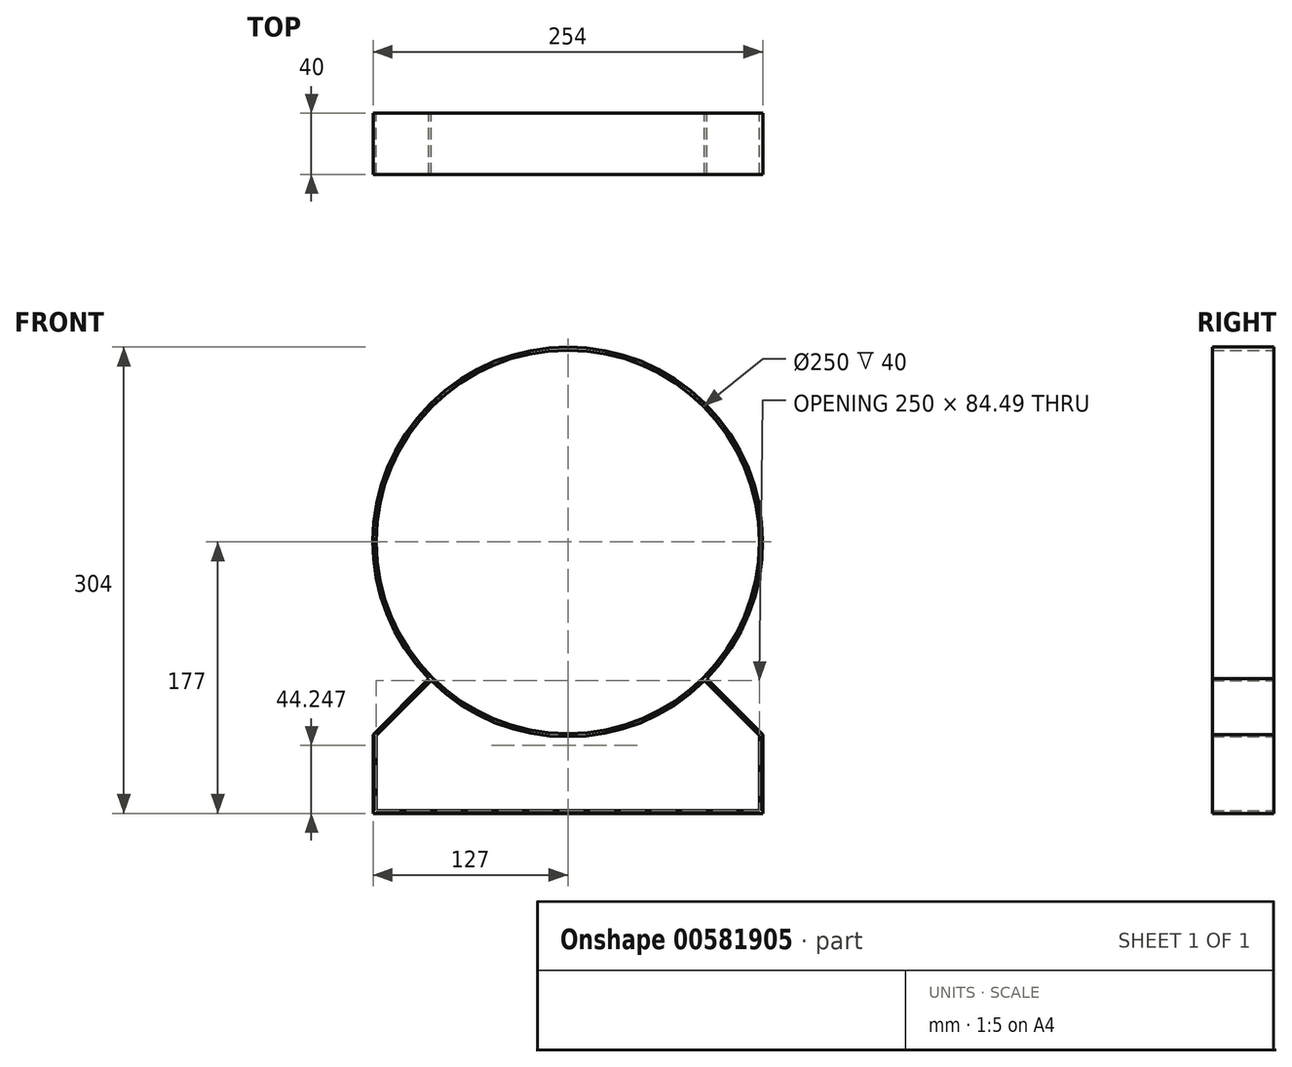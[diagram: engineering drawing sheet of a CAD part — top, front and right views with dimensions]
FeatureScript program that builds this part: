
annotation { "Feature Type Name" : "Feature", "Feature Type Description" : "" }
export const myFeature = defineFeature(function(context is Context, id is Id, definition is map)
    precondition{}
    {
        {
            var Q0;
            Q0=qCreatedBy(makeId("Front.planeOp"),FACE);
            var sketch = newSketch(context, id + "F0", { "sketchPlane" : qUnion([Q0])});
            skLineSegment(sketch, "E0", {"start": v(0, 0) * mm, "end": v(-679.96, 0) * mm, "construction": true});
            skLineSegment(sketch, "E1", {"start": v(0, 0) * mm, "end": v(0, 658.78) * mm, "construction": true});
            skLineSegment(sketch, "E2", {"start": v(0, 0) * mm, "end": v(-291.77, -291.77) * mm, "construction": true});
            skLineSegment(sketch, "E3", {"start": v(0, 0) * mm, "end": v(291.77, -291.77) * mm, "construction": true});
            skCircle(sketch, "E4", {"center": v(0, 0) * mm, "radius": 125 * mm});
            skCircle(sketch, "E5", {"center": v(0, 0) * mm, "radius": 127 * mm});
            skLineSegment(sketch, "E6", {"start": v(-127, -177) * mm, "end": v(0, -177) * mm});
            skLineSegment(sketch, "E7", {"start": v(-125, -175) * mm, "end": v(0, -175) * mm});
            skLineSegment(sketch, "E8", {"start": v(0, 0) * mm, "end": v(0, -311.11) * mm, "construction": true});
            skLineSegment(sketch, "E9", {"start": v(-125, -175) * mm, "end": v(-125, -126.41) * mm});
            skLineSegment(sketch, "E10", {"start": v(-127, -177) * mm, "end": v(-127, -125.59) * mm});
            skLineSegment(sketch, "E11", {"start": v(-90.5, -89.1) * mm, "end": v(-127, -125.59) * mm});
            skLineSegment(sketch, "E12", {"start": v(-89.1, -90.5) * mm, "end": v(-125, -126.41) * mm});
            skLineSegment(sketch, "E13.MirrorCS", {"start": v(89.1, -90.5) * mm, "end": v(125, -126.41) * mm});
            skLineSegment(sketch, "E14.MirrorCS", {"start": v(127, -177) * mm, "end": v(0, -177) * mm});
            skLineSegment(sketch, "E15.MirrorCS", {"start": v(125, -175) * mm, "end": v(0, -175) * mm});
            skLineSegment(sketch, "E16.MirrorCS", {"start": v(90.5, -89.1) * mm, "end": v(127, -125.59) * mm});
            skLineSegment(sketch, "E17.MirrorCS", {"start": v(125, -175) * mm, "end": v(125, -126.41) * mm});
            skLineSegment(sketch, "E18.MirrorCS", {"start": v(127, -177) * mm, "end": v(127, -125.59) * mm});
            skSolve(sketch);
        }
        {
            var Q0;
            Q0=qSketchRegion(id+"F0",true);
            extrude(context, id + "F1", {"entities" : qUnion([Q0]), "offsetDistance" : 25 * mm, "depth" : 40 * mm});
        }
    });
